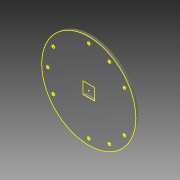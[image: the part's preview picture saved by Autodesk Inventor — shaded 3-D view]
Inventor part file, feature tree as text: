
AUTODESK INVENTOR PART (.ipt)
format: ipt  version: 2015 (Build 190159000, 159)  size: 132,608 bytes
history: native  units: mm
features: sketch x3, extrude x2, projected_geometry x2
ambient origin geometry x8: Origin, YZ Plane, XZ Plane, XY Plane, X Axis, Y Axis, Z Axis, Center Point
bodies: Solid1 (feature_tree)
feature tree (7):
  extrude  "Extrusion1"  Depth=12.8mm
  extrude  "Extrusion2"  Depth=3.0mm TaperAngle=0.0deg
  sketch  "Sketch3"  dims[d5=120.0deg d6=120.0deg d7=90.0mm d8=30.0deg d9=30.0deg d10=30.0deg d11=30.0deg d12=30.0deg d13=30.0deg d14=30.0deg d15=30.0deg d16=3.0mm d17=3.0mm d18=3.0mm d19=3.0mm d20=3.0mm d21=3.0mm d22=3.0mm d23=3.0mm d24=3.0mm d25=3.0mm d26=0.0mm]
  sketch  "Sketch1"  dims[d0=103.0mm d1=12.8mm]
  sketch  "Sketch2"  dims[d2=12.8mm d3=3.0mm d4=0.0mm]
  projected_geometry  "Projected Loop1"
  projected_geometry  "Projected Loop2"
